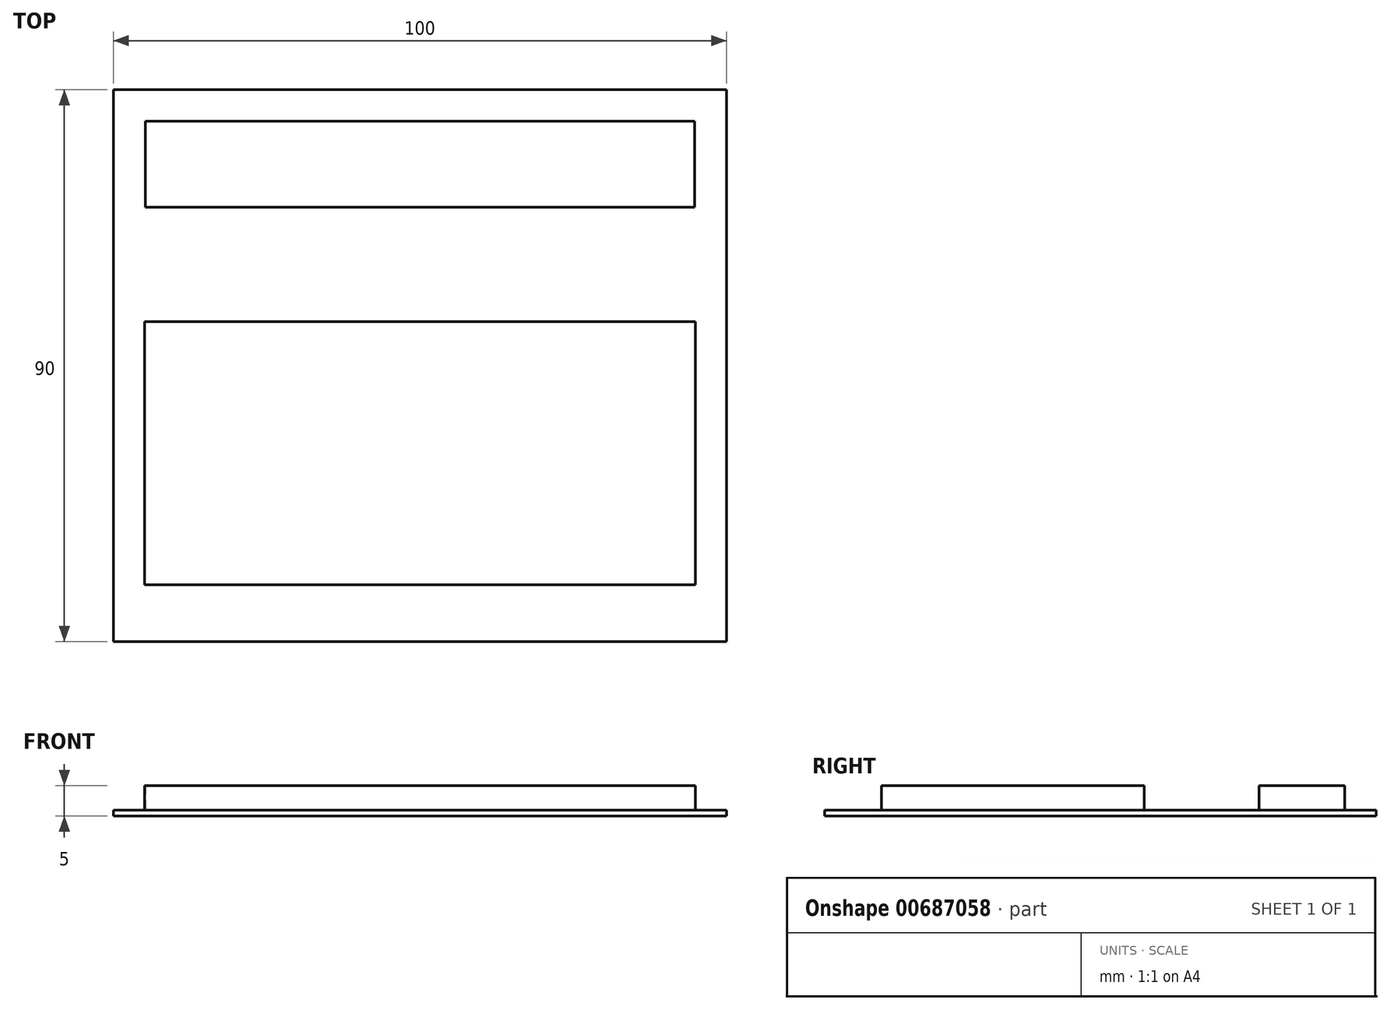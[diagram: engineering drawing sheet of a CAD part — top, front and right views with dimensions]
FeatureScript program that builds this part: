
annotation { "Feature Type Name" : "Feature", "Feature Type Description" : "" }
export const myFeature = defineFeature(function(context is Context, id is Id, definition is map)
    precondition{}
    {
        {
            var Q0;
            Q0=qCreatedBy(makeId("Top.planeOp"),FACE);
            var sketch = newSketch(context, id + "F0", { "sketchPlane" : qUnion([Q0])});
            skLineSegment(sketch, "E0.bottom", {"start": v(-100, 90) * mm, "end": v(0, 90) * mm});
            skLineSegment(sketch, "E0.top", {"start": v(-100, 0) * mm, "end": v(0, 0) * mm});
            skLineSegment(sketch, "E0.left", {"start": v(-100, 90) * mm, "end": v(-100, 0) * mm});
            skLineSegment(sketch, "E0.right", {"start": v(0, 90) * mm, "end": v(0, 0) * mm});
            skSolve(sketch);
        }
        {
            var Q0;
            Q0=makeQuery(id+"F0.imprint","IMPRINT",FACE,{"disambiguationData":[TD([[makeQuery(id+"F0.imprint","IMPRINT",EDGE,{"derivedFrom":sQuery(id+"F0.wireOp",EDGE,"E0.bottom")}),-1.0]])]});
            extrude(context, id + "F1", {"entities" : qUnion([Q0]), "depth" : 1 * mm, "offsetDistance" : 25.4 * mm});
        }
        {
            var Q0;
            Q0=qCreatedBy(makeId("Top.planeOp"),FACE);
            var sketch = newSketch(context, id + "F2", { "sketchPlane" : qUnion([Q0])});
            skLineSegment(sketch, "E1.bottom", {"start": v(-94.82, 84.87) * mm, "end": v(-5.2, 84.87) * mm});
            skLineSegment(sketch, "E1.top", {"start": v(-94.82, 70.87) * mm, "end": v(-5.2, 70.87) * mm});
            skLineSegment(sketch, "E1.left", {"start": v(-94.82, 84.87) * mm, "end": v(-94.82, 70.87) * mm});
            skLineSegment(sketch, "E1.right", {"start": v(-5.2, 84.87) * mm, "end": v(-5.2, 70.87) * mm});
            skSolve(sketch);
        }
        {
            var Q0;
            Q0 = qSketchRegion(id + "F2", true);
            extrude(context, id + "F3", {"entities" : qUnion([Q0]), "operationType" : NewBodyOperationType.ADD, "depth" : 5 * mm, "offsetDistance" : 25.4 * mm});
        }
        {
            var Q0;
            Q0=qCreatedBy(makeId("Top.planeOp"),FACE);
            var sketch = newSketch(context, id + "F4", { "sketchPlane" : qUnion([Q0])});
            skLineSegment(sketch, "E2.bottom", {"start": v(-94.91, 52.15) * mm, "end": v(-5.1, 52.15) * mm});
            skLineSegment(sketch, "E2.top", {"start": v(-94.91, 9.25) * mm, "end": v(-5.1, 9.25) * mm});
            skLineSegment(sketch, "E2.left", {"start": v(-94.91, 52.15) * mm, "end": v(-94.91, 9.25) * mm});
            skLineSegment(sketch, "E2.right", {"start": v(-5.1, 52.15) * mm, "end": v(-5.1, 9.25) * mm});
            skSolve(sketch);
        }
        {
            var Q0;
            Q0 = qSketchRegion(id + "F4", true);
            extrude(context, id + "F5", {"entities" : qUnion([Q0]), "operationType" : NewBodyOperationType.ADD, "depth" : 5 * mm, "offsetDistance" : 25.4 * mm});
        }
    });
